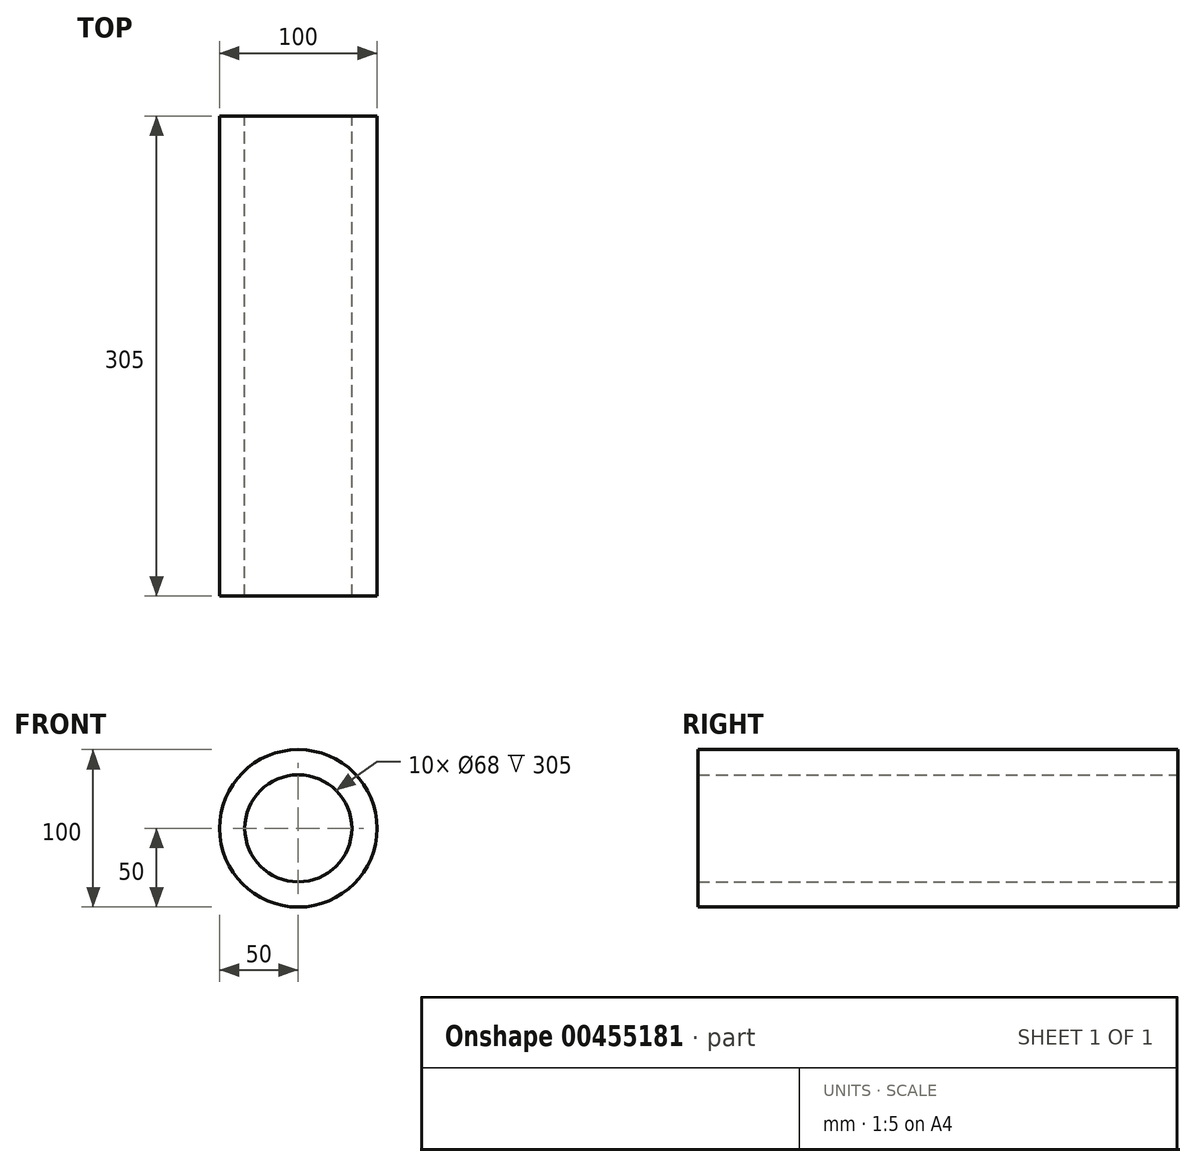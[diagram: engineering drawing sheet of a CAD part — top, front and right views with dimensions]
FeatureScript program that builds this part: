
annotation { "Feature Type Name" : "Feature", "Feature Type Description" : "" }
export const myFeature = defineFeature(function(context is Context, id is Id, definition is map)
    precondition{}
    {
        {
            var Q0;
            Q0=qCreatedBy(makeId("Front.planeOp"),FACE);
            var sketch = newSketch(context, id + "F0", { "sketchPlane" : qUnion([Q0])});
            skCircle(sketch, "E0", {"center": v(0, 0) * mm, "radius": 34 * mm});
            skCircle(sketch, "E1", {"center": v(0, 0) * mm, "radius": 50 * mm});
            skSolve(sketch);
        }
        {
            var Q0;
            Q0 = qSketchRegion(id + "F0", true);
            extrude(context, id + "F1", {"entities" : qUnion([Q0]), "depth" : 305 * mm});
        }
    });
